# Revit family: V-THRM_NAM_CWA_CA-80-ME.rfa
name_source: partatom
category: Mechanical Equipment
units: mm (PartAtom-declared; Revit-internal decimal feet)

## family parameters
Always vertical = Yes
Cut with Voids When Loaded = No
OmniClass Number = 23.75.00.00
OmniClass Title = Climate Control (HVAC)
Part Type = Normal
Room Calculation Point = No
Round Connector Dimension = Use Diameter
Shared = No
Work Plane-Based = No

## types (1)
- Condensing Pump
    Apparent Load = 0 VA
    Body Material = Paint Vertiv Black
    Clearance Material = Clearance
    Default Elevation = 0 "
    Depth = 59.4 "
    Filter Material = Filters Vertiv
    Flange Material = Copper
    Frequency = 0 Hz
    Full Load Current = 0 A
    Grille Material = Grille metal Vertiv
    Height = 144.48 "
    Manufacturer = Liebert
    Model = CWA CA80
    Number of Poles = 1
    Overcurrent Protection Device = 0 A
    Phase = 1
    Pipe Material = Copper
    Power Factor = 0
    Protective Grill Material = Aluminium
    Voltage = 0 V
    Width = 155.95 "

## geometry (parser evidence)
native form markers: Sweep x35
no freeform markers — native parametric forms only
